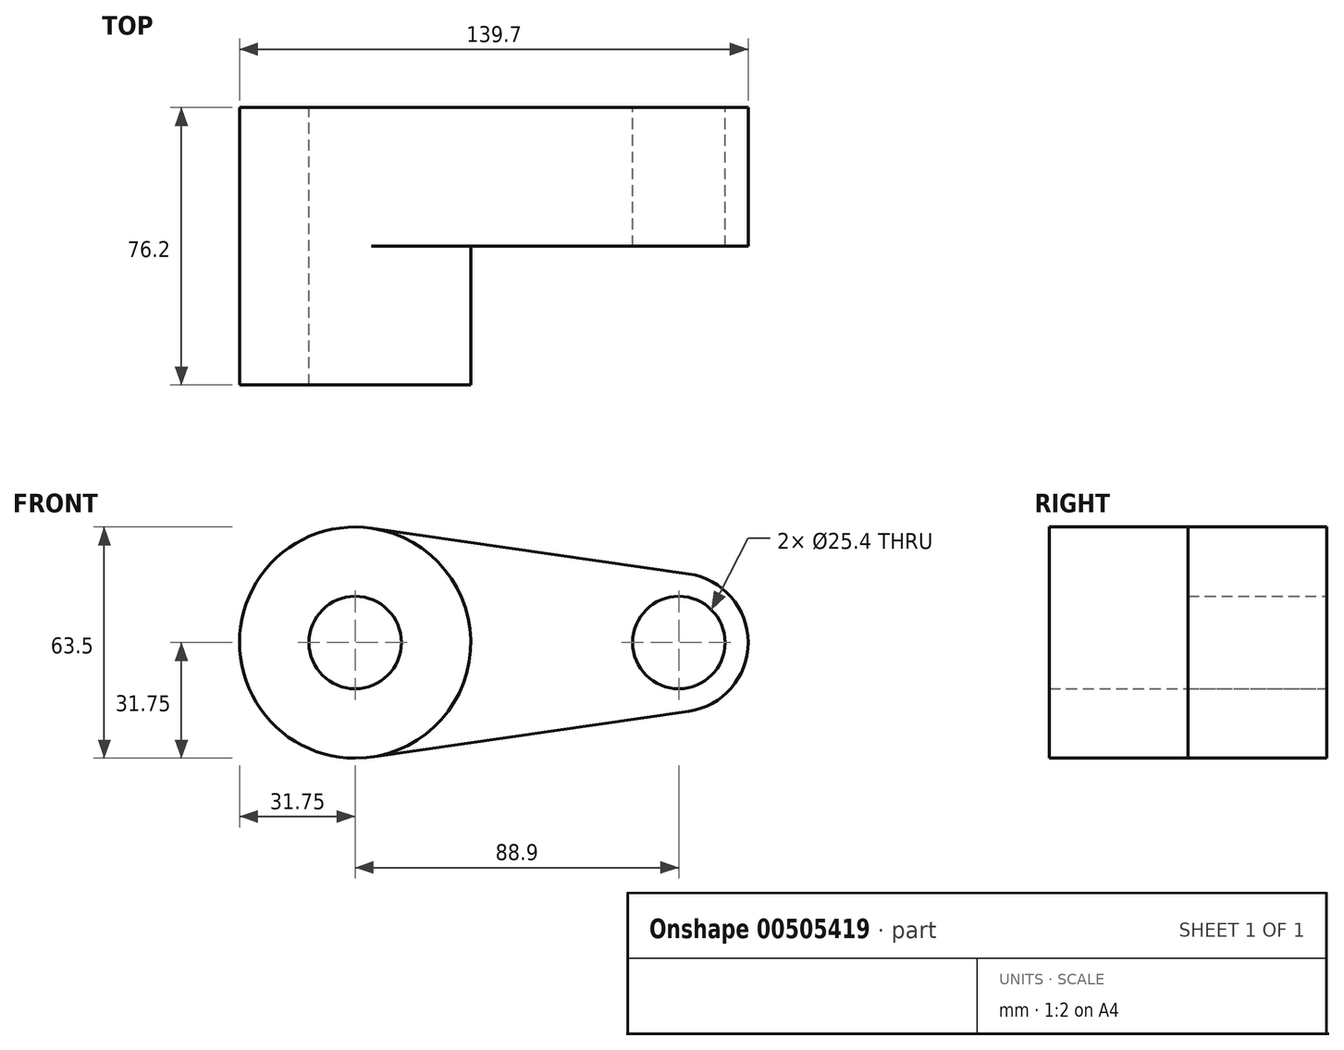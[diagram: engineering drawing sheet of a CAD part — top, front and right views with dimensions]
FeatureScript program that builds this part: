
annotation { "Feature Type Name" : "Feature", "Feature Type Description" : "" }
export const myFeature = defineFeature(function(context is Context, id is Id, definition is map)
    precondition{}
    {
        {
            var Q0;
            Q0=qCreatedBy(makeId("Front.planeOp"),FACE);
            var sketch = newSketch(context, id + "F0", { "sketchPlane" : qUnion([Q0])});
            skCircle(sketch, "E0", {"center": v(0, 0) * mm, "radius": 31.75 * mm});
            skCircle(sketch, "E1", {"center": v(88.9, 0) * mm, "radius": 19.05 * mm});
            skLineSegment(sketch, "E2", {"start": v(4.54, 31.42) * mm, "end": v(91.62, 18.85) * mm});
            skLineSegment(sketch, "E3", {"start": v(4.54, -31.42) * mm, "end": v(91.62, -18.85) * mm});
            skCircle(sketch, "E4", {"center": v(0, 0) * mm, "radius": 12.7 * mm});
            skCircle(sketch, "E5", {"center": v(88.9, 0) * mm, "radius": 12.7 * mm});
            skSolve(sketch);
        }
        {
            var Q0;
            Q0=makeQuery(id+"F0.imprint","IMPRINT",FACE,{"disambiguationData":[TD([[makeQuery(id+"F0.imprint","IMPRINT",EDGE,{"derivedFrom":sQuery(id+"F0.wireOp",EDGE,"E4")}),-1.0]])]});
            var Q1;
            {var subQ0=sQuery(id+"F0.wireOp",EDGE,"E2");Q1=makeQuery(id+"F0.imprint","IMPRINT",FACE,{"disambiguationData":[TD([[makeQuery(id+"F0.imprint","IMPRINT",EDGE,{"derivedFrom":subQ0}),-1.0]])]});}
            var Q2;
            Q2=makeQuery(id+"F0.imprint","IMPRINT",FACE,{"disambiguationData":[TD([[makeQuery(id+"F0.imprint","IMPRINT",EDGE,{"derivedFrom":sQuery(id+"F0.wireOp",EDGE,"E5")}),-1.0]])]});
            extrude(context, id + "F1", {"entities" : qUnion([Q0, Q1, Q2]), "depth" : 38.1 * mm});
        }
        {
            var Q0;
            Q0=makeQuery(id+"F0.imprint","IMPRINT",FACE,{"disambiguationData":[TD([[makeQuery(id+"F0.imprint","IMPRINT",EDGE,{"derivedFrom":sQuery(id+"F0.wireOp",EDGE,"E4")}),-1.0]])]});
            extrude(context, id + "F2", {"entities" : qUnion([Q0]), "operationType" : NewBodyOperationType.ADD, "depth" : 76.2 * mm});
        }
    });
